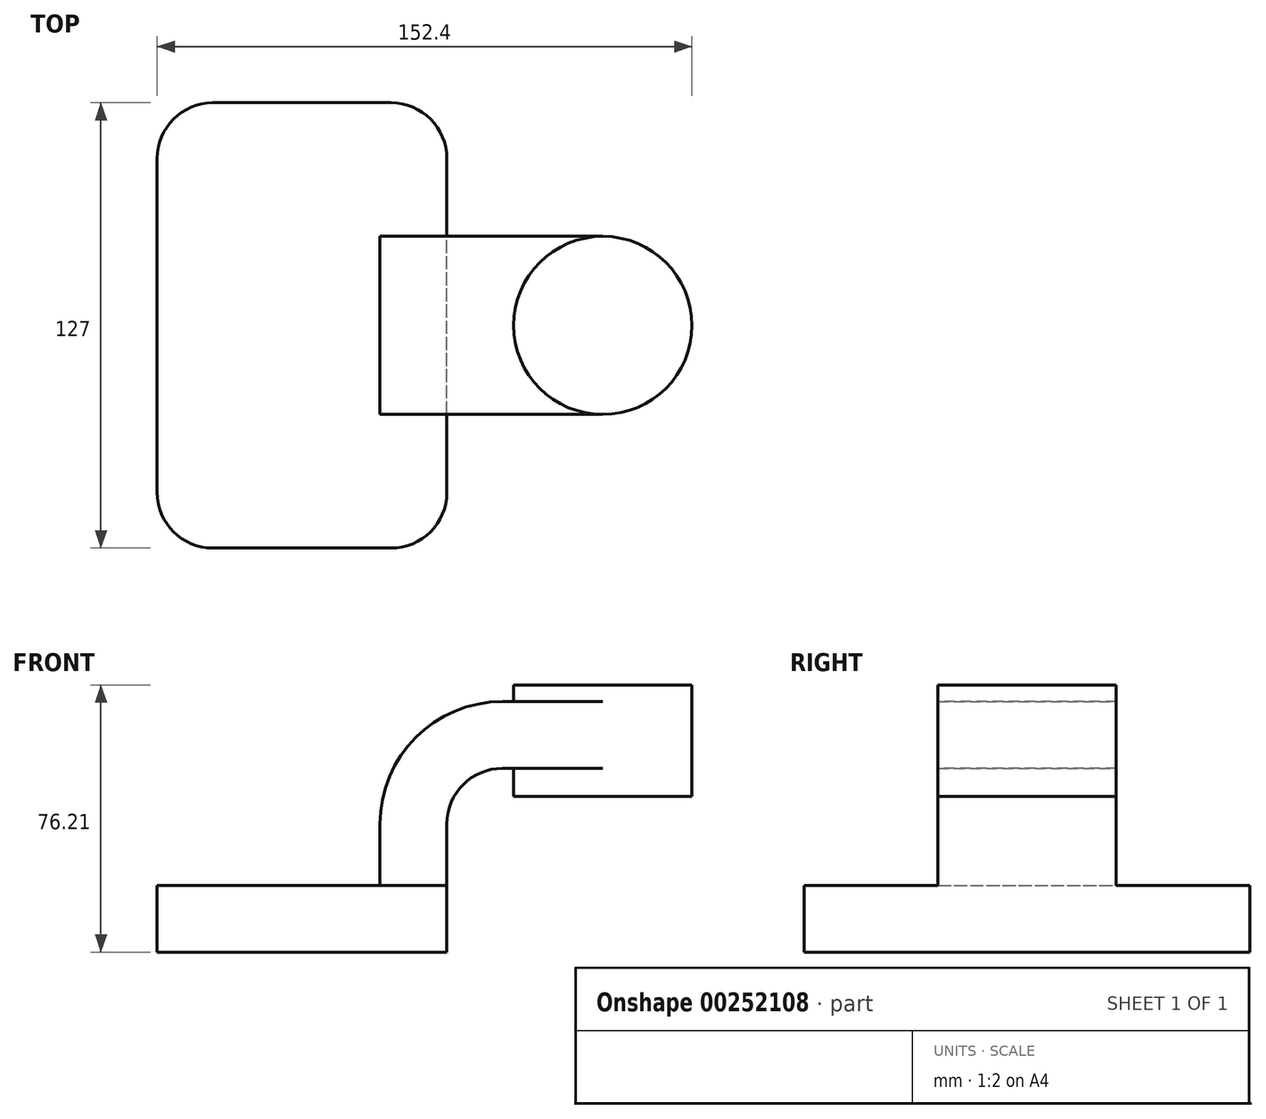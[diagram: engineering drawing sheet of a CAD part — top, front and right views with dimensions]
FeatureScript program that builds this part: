
annotation { "Feature Type Name" : "Feature", "Feature Type Description" : "" }
export const myFeature = defineFeature(function(context is Context, id is Id, definition is map)
    precondition{}
    {
        {
            var Q0;
            Q0=qCreatedBy(makeId("Front.planeOp"),FACE);
            var sketch = newSketch(context, id + "F0", { "sketchPlane" : qUnion([Q0])});
            skLineSegment(sketch, "E0.bottom", {"start": v(41.27, 9.53) * mm, "end": v(-41.28, 9.53) * mm});
            skLineSegment(sketch, "E0.top", {"start": v(41.28, -9.52) * mm, "end": v(-41.27, -9.52) * mm});
            skLineSegment(sketch, "E0.left", {"start": v(41.27, 9.53) * mm, "end": v(41.28, -9.52) * mm});
            skLineSegment(sketch, "E0.right", {"start": v(-41.28, 9.53) * mm, "end": v(-41.27, -9.52) * mm});
            skPoint(sketch, "E0.middle", {"position": v(0, 0) * mm});
            skLineSegment(sketch, "E1.bottom", {"start": v(60.32, 34.93) * mm, "end": v(111.12, 34.93) * mm});
            skLineSegment(sketch, "E1.top", {"start": v(60.32, 66.68) * mm, "end": v(111.12, 66.68) * mm});
            skLineSegment(sketch, "E1.left", {"start": v(60.32, 34.93) * mm, "end": v(60.32, 66.68) * mm});
            skLineSegment(sketch, "E1.right", {"start": v(111.12, 34.93) * mm, "end": v(111.12, 66.68) * mm});
            skPoint(sketch, "E1.middle", {"position": v(85.72, 50.8) * mm});
            skLineSegment(sketch, "E2", {"start": v(41.27, 9.53) * mm, "end": v(41.27, 27) * mm});
            skArc(sketch, "E3", {"start": v(41.27, 27) * mm, "mid": v(45.92, 38.23) * mm, "end": v(57.15, 42.88) * mm});
            skLineSegment(sketch, "E4", {"start": v(57.15, 42.88) * mm, "end": v(85.72, 42.88) * mm});
            skLineSegment(sketch, "E5.0", {"start": v(57.15, 61.93) * mm, "end": v(85.72, 61.93) * mm});
            skArc(sketch, "E5.1", {"start": v(22.22, 27) * mm, "mid": v(32.45, 51.7) * mm, "end": v(57.15, 61.93) * mm});
            skLineSegment(sketch, "E5.2", {"start": v(22.22, 9.53) * mm, "end": v(22.22, 27) * mm});
            skFitSpline(sketch, "E6", {"points": [v(-41.28, 9.53) * mm, v(57.15, 61.93) * mm], "startDerivative": vector(0, 76.2) * mm, "endDerivative": vector(171.45, 0) * mm});
            skLineSegment(sketch, "E7", {"start": v(85.72, 66.68) * mm, "end": v(85.72, 34.93) * mm});
            skSolve(sketch);
        }
        {
            var Q0;
            Q0=makeQuery(id+"F0.imprint","IMPRINT",FACE,{"disambiguationData":[TD([[makeQuery(id+"F0.imprint","IMPRINT",EDGE,{"derivedFrom":sQuery(id+"F0.wireOp",EDGE,"E0.top")}),-1.0]])]});
            extrude(context, id + "F1", {"entities" : qUnion([Q0]), "endBound" : BoundingType.SYMMETRIC, "depth" : 127 * mm});
        }
        {
            var Q0;
            Q0=makeQuery(id+"F0.imprint","IMPRINT",FACE,{"disambiguationData":[TD([[makeQuery(id+"F0.imprint","IMPRINT",EDGE,{"derivedFrom":sQuery(id+"F0.wireOp",EDGE,"E0.top")}),-1.0]])]});
            var Q1;
            {var subQ1=sQuery(id+"F0.wireOp",EDGE,"E2");Q1=makeQuery(id+"F0.imprint","IMPRINT",FACE,{"disambiguationData":[TD([[makeQuery(id+"F0.imprint","IMPRINT",EDGE,{"derivedFrom":subQ1}),1.0]])]});}
            var Q2;
            {var subQ0=sQuery(id+"F0.wireOp",EDGE,"E4");var subQ1=sQuery(id+"F0.wireOp",EDGE,"E1.left");var subQ2=makeQuery(id+"F0.imprint","INTERSECT",VERTEX,{"derivedFrom":[subQ1,subQ0]});Q2=makeQuery(id+"F0.imprint","IMPRINT",FACE,{"disambiguationData":[TD([[makeQuery(id+"F0.imprint","IMPRINT",EDGE,{"disambiguationData":[TD([[subQ2,-1.0]])],"derivedFrom":subQ1}),-1.0]])]});}
            extrude(context, id + "F2", {"entities" : qUnion([Q0, Q1, Q2]), "operationType" : NewBodyOperationType.ADD, "endBound" : BoundingType.SYMMETRIC, "depth" : 50.8 * mm});
        }
        {
            var Q0;
            Q0=makeQuery(id+"F0.imprint","IMPRINT",FACE,{"disambiguationData":[TD([[makeQuery(id+"F0.imprint","IMPRINT",EDGE,{"derivedFrom":sQuery(id+"F0.wireOp",EDGE,"E5.1")}),1.0]])]});
            extrude(context, id + "F3", {"entities" : qUnion([Q0]), "operationType" : NewBodyOperationType.ADD, "endBound" : BoundingType.SYMMETRIC, "depth" : 15.88 * mm});
        }
        {
            var Q0;
            {var subQ0=sQuery(id+"F0.wireOp",EDGE,"E1.right");Q0=makeQuery(id+"F0.imprint","IMPRINT",FACE,{"disambiguationData":[TD([[makeQuery(id+"F0.imprint","IMPRINT",EDGE,{"derivedFrom":subQ0}),1.0]])]});}
            var Q1;
            Q1=sQuery(id+"F0.wireOp",EDGE,"E7");
            revolve(context, id + "F4", {"operationType" : NewBodyOperationType.ADD, "entities" : qUnion([Q0]), "axis" : qUnion([Q1]), "revolveType" : RevolveType.FULL});
        }
        {
            var Q0;
            Q0=makeQuery(id+"F1.opExtrude","CAP_EDGE",EDGE,{"disambiguationData":[OSD([sQuery(id+"F0.wireOp",EDGE,"E0.left")])],"isStart":false});
            var Q1;
            Q1=makeQuery(id+"F1.opExtrude","CAP_EDGE",EDGE,{"disambiguationData":[OSD([sQuery(id+"F0.wireOp",EDGE,"E0.right")])],"isStart":false});
            var Q2;
            Q2=makeQuery(id+"F1.opExtrude","CAP_EDGE",EDGE,{"disambiguationData":[OSD([sQuery(id+"F0.wireOp",EDGE,"E0.right")])],"isStart":true});
            var Q3;
            Q3=makeQuery(id+"F1.opExtrude","CAP_EDGE",EDGE,{"disambiguationData":[OSD([sQuery(id+"F0.wireOp",EDGE,"E0.left")])],"isStart":true});
            fillet(context, id + "F5", {"entities" : qUnion([Q0, Q1, Q2, Q3]), "radius" : 15.88 * mm, "tangentPropagation" : true, "allowEdgeOverflow" : false});
        }
    });
